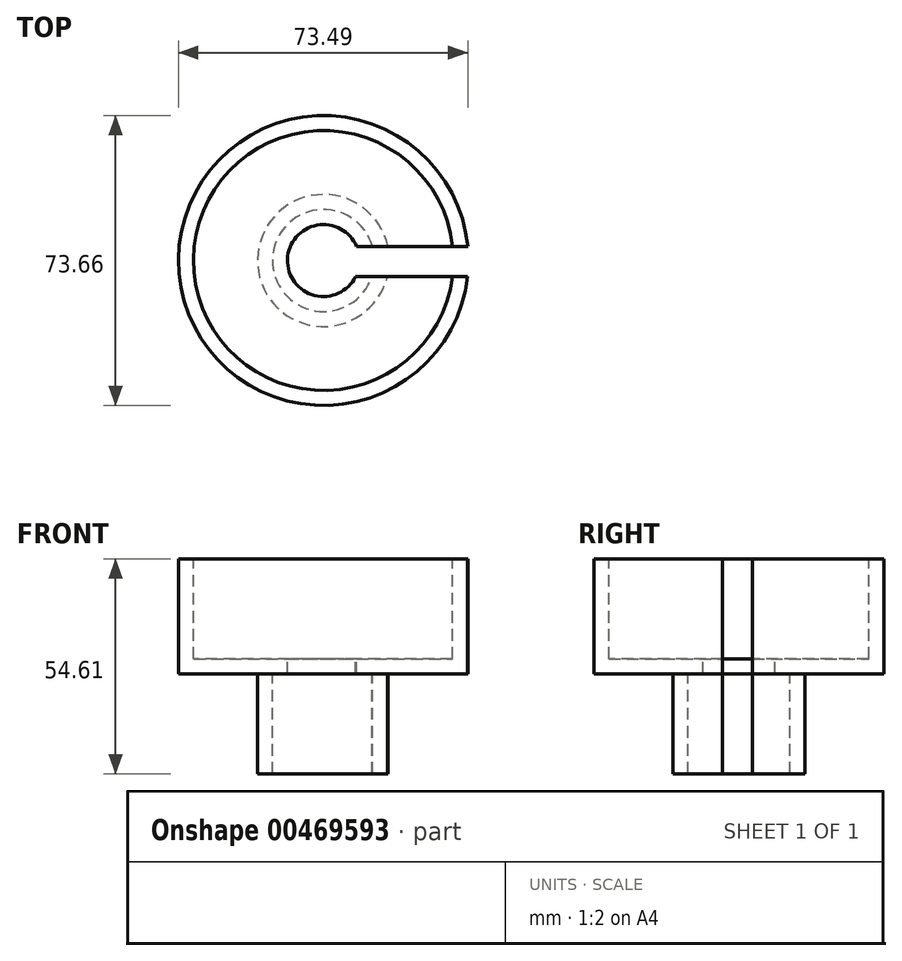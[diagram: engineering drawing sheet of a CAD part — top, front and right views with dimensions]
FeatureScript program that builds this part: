
annotation { "Feature Type Name" : "Feature", "Feature Type Description" : "" }
export const myFeature = defineFeature(function(context is Context, id is Id, definition is map)
    precondition{}
    {
        {
            var Q0;
            Q0=qCreatedBy(makeId("Front.planeOp"),FACE);
            var sketch = newSketch(context, id + "F0", { "sketchPlane" : qUnion([Q0])});
            skLineSegment(sketch, "E0", {"start": v(12.95, -29.21) * mm, "end": v(12.95, -3.8) * mm});
            skLineSegment(sketch, "E1", {"start": v(12.95, -3.8) * mm, "end": v(9.14, -3.8) * mm});
            skLineSegment(sketch, "E2", {"start": v(9.14, -3.81) * mm, "end": v(9.14, 0) * mm});
            skLineSegment(sketch, "E3", {"start": v(9.14, 0) * mm, "end": v(33.02, 0) * mm});
            skLineSegment(sketch, "E4", {"start": v(33.02, 0) * mm, "end": v(33.02, 25.4) * mm});
            skLineSegment(sketch, "E5", {"start": v(33.02, 25.4) * mm, "end": v(36.83, 25.4) * mm});
            skLineSegment(sketch, "E6", {"start": v(36.83, 25.4) * mm, "end": v(36.83, -3.8) * mm});
            skLineSegment(sketch, "E7", {"start": v(36.83, -3.8) * mm, "end": v(16.76, -3.8) * mm});
            skLineSegment(sketch, "E8", {"start": v(16.76, -3.81) * mm, "end": v(16.76, -29.21) * mm});
            skLineSegment(sketch, "E9", {"start": v(16.76, -29.21) * mm, "end": v(12.95, -29.21) * mm});
            skSolve(sketch);
        }
        {
            var Q0;
            Q0=qCreatedBy(makeId("Front.planeOp"),FACE);
            var sketch = newSketch(context, id + "F1", { "sketchPlane" : qUnion([Q0])});
            skLineSegment(sketch, "E10", {"start": v(0, 0) * mm, "end": v(0, -18.9) * mm});
            skSolve(sketch);
        }
        {
            var Q0;
            Q0=makeQuery(id+"F0.imprint","IMPRINT",FACE,{"disambiguationData":[TD([[makeQuery(id+"F0.imprint","IMPRINT",EDGE,{"derivedFrom":sQuery(id+"F0.wireOp",EDGE,"E0")}),-1.0]])]});
            var Q1;
            Q1=sQuery(id+"F1.wireOp",EDGE,"E10");
            revolve(context, id + "F2", {"entities" : qUnion([Q0]), "axis" : qUnion([Q1]), "revolveType" : RevolveType.FULL});
        }
        {
            var Q0;
            Q0=makeQuery(id+"F2.opRevolve","SWEPT_FACE",FACE,{"disambiguationData":[OSD([sQuery(id+"F0.wireOp",EDGE,"E5")])]});
            var sketch = newSketch(context, id + "F3", { "sketchPlane" : qUnion([Q0])});
            skLineSegment(sketch, "E11", {"start": v(0, 0) * mm, "end": v(0, 3.54) * mm});
            skLineSegment(sketch, "E12", {"start": v(0, 3.54) * mm, "end": v(38.1, 3.54) * mm});
            skLineSegment(sketch, "E13", {"start": v(38.1, 3.54) * mm, "end": v(38.1, -4.08) * mm});
            skLineSegment(sketch, "E14", {"start": v(38.1, -4.08) * mm, "end": v(0, -4.08) * mm});
            skLineSegment(sketch, "E15", {"start": v(0, -4.08) * mm, "end": v(0, 0) * mm});
            skSolve(sketch);
        }
        {
            var Q0;
            Q0 = qSketchRegion(id + "F3", true);
            extrude(context, id + "F4", {"entities" : qUnion([Q0]), "operationType" : NewBodyOperationType.REMOVE, "endBound" : BoundingType.THROUGH_ALL, "oppositeDirection" : true, "depth" : 25.4 * mm});
        }
    });
